# Revit family: UNB_Specchio_Multiproduct_BIM_IT_T3373;T3388;T3389;T3425_NEW
name_source: partatom
category: Plumbing Fixtures
revit_build: Autodesk Revit 2017 (Build: 20160225_1515(x64)
units: mm (PartAtom-declared; Revit-internal decimal feet)

## family parameters
Cut with Voids When Loaded = No
Host = Face
Part Type = Normal
Room Calculation Point = No
Round Connector Dimension = Use Diameter
Shared = No

## types (4) — shared parameters
Accessori = http://www.idealstandard.it
AltezzaNominale = 730 mm  [stored 2.39501 ft]
Autore = Ideal Standard
Brand = Ideal Standard
CodiceDiPrestazione = EN
Colore = specchio
Connessione = piombatura
Default Elevation = 1500 mm  [stored 4.92126 ft]
DescrizioneClassifcazioneUni2015 = Bathroom furniture
Finitura = specchio
Forma = rettangolare
Garanzia = garanzia del produttore
IfcEsportaCome = BATHROOM FURNITURE
InformazioniDiProdotto = http://www.idealstandard.it
InstruzioniInstallazione = http://www.idealstandard.it
LunghezzaNominale = 170 mm  [stored 0.557743 ft]
Materiale = bicchiere
PartiDiRicambio = http://www.idealstandard.it
ProfonditàNominale = 170 mm  [stored 0.557743 ft]
Revisione = 1
RiferimentoClassificazioneUni2015 = MIRRORS
Spazio = interno
Telefono = 800 652 290
TipoDiDato = Fisso
TipoEspotazioneIfc = IfcFurnitureType
TipologiaVaso = Altro
URL = http://www.idealstandard.it
UnitàDurata = anno
UnitàDurataGaranzia = anno
UnitàLineare = millimetro
UnitàMonetaria = €
UnitàSuperficie = millimetro
UnitàVolume = litro
Versione = 1
VersioneClassificazioneUni2015 = IfcFurnitureType
zero-valued in all types: Cost, CostoDiSostituzione

## per-type parameters (varying)
| type | Caratteristiche | CodiceABarre | Description | DoubleUnitsOnly | LarghezzaNominale | Model | ModelloDiRiferimento | Nome | NomeOggettoBim | NumeroDiModello | PesoNetto | Riferimento | SingleUnitsOnly |
| T3373 - 600 x 700 mirror cabinet | SPECCHIO CONT. HIGH 60X70 MATT AL 20W 23 | 8014140447658 | SPECCHIO CONT. HIGH 60X70 MATT AL 20W 23 | No | 630 mm  [stored 2.06693 ft] | T3373AL | SPECCHIO CONT. HIGH 60X70 MATT AL 20W 23 | ISI_IdealStandard_Specchio_T3373 | ISI_IdealStandard_Specchio_T3373 | T3373AL | 20.00 Kg | T3373 | Yes |
| T3388 - 800 x 700 mirror cabinet | SPECCHIO CONT. HIGH 80X70 MATT AL 20W 23 | 8014140447696 | SPECCHIO CONT. HIGH 80X70 MATT AL 20W 23 | Yes | 830 mm  [stored 2.7231 ft] | T3388AL | SPECCHIO CONT. HIGH 80X70 MATT AL 20W 23 | ISI_IdealStandard_Specchio_T3388 | ISI_IdealStandard_Specchio_T3388 | T3388AL | 24.00 Kg | T3388 | No |
| T3389 - 1000 x 700 mirror cabinet | SPECCHIO CONT. HIGH 100X70 MATT AL 20W 2 | 8014140447719 | SPECCHIO CONT. HIGH 100X70 MATT AL 20W 2 | Yes | 1030 mm  [stored 3.37927 ft] | T3389AL | SPECCHIO CONT. HIGH 100X70 MATT AL 20W 2 | ISI_IdealStandard_Specchio_T3389 | ISI_IdealStandard_Specchio_T3389 | T3389AL | 26.00 Kg | T3389 | No |
| T3425 - 1200 x 700 mirror cabinet | SPECCHIO CONT. HIGH 120X70 MATT AL 20W 2 | 8014140447733 | SPECCHIO CONT. HIGH 120X70 MATT AL 20W 2 | Yes | 1230 mm  [stored 4.03543 ft] | T3425AL | SPECCHIO CONT. HIGH 120X70 MATT AL 20W 2 | ISI_IdealStandard_Specchio_T3425 | ISI_IdealStandard_Specchio_T3425 | T3425AL | 30.00 Kg | T3425 | No |

note: [stored X ft] marks values corroborated as IEEE doubles in the binary element streams (Revit-internal decimal feet)

## geometry (parser evidence)
native form markers: Sweep x1
no freeform markers — native parametric forms only
